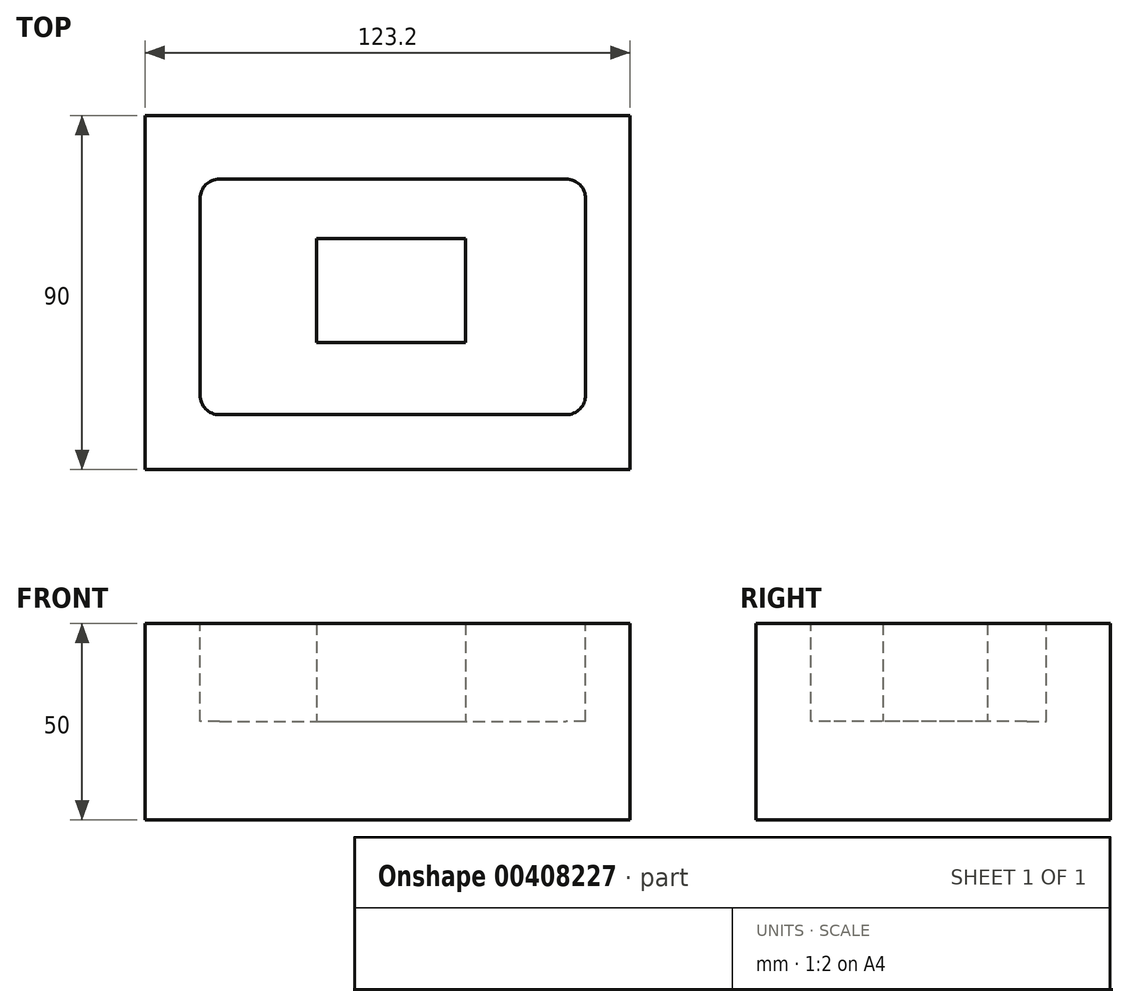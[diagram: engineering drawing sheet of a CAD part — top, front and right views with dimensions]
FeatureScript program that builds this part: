
annotation { "Feature Type Name" : "Feature", "Feature Type Description" : "" }
export const myFeature = defineFeature(function(context is Context, id is Id, definition is map)
    precondition{}
    {
        {
            var Q0;
            Q0=qCreatedBy(makeId("Top.planeOp"),FACE);
            var sketch = newSketch(context, id + "F0", { "sketchPlane" : qUnion([Q0])});
            skLineSegment(sketch, "E0.bottom", {"start": v(-60.6, 50.44) * mm, "end": v(62.6, 50.44) * mm});
            skLineSegment(sketch, "E0.top", {"start": v(-60.6, -39.56) * mm, "end": v(62.6, -39.56) * mm});
            skLineSegment(sketch, "E0.left", {"start": v(-60.6, 50.44) * mm, "end": v(-60.6, -39.56) * mm});
            skLineSegment(sketch, "E0.right", {"start": v(62.6, 50.44) * mm, "end": v(62.6, -39.56) * mm});
            skSolve(sketch);
        }
        {
            var Q0;
            Q0=makeQuery(id+"F0.imprint","IMPRINT",FACE,{"disambiguationData":[TD([[makeQuery(id+"F0.imprint","IMPRINT",EDGE,{"derivedFrom":sQuery(id+"F0.wireOp",EDGE,"E0.bottom")}),-1.0]])]});
            extrude(context, id + "F1", {"entities" : qUnion([Q0]), "depth" : 50 * mm});
        }
        {
            var Q0;
            Q0=makeQuery(id+"F1.opExtrude","CAP_FACE",FACE,{"disambiguationData":[OSD([sQuery(id+"F0.wireOp",EDGE,"E0.bottom"),sQuery(id+"F0.wireOp",EDGE,"E0.top"),sQuery(id+"F0.wireOp",EDGE,"E0.left"),sQuery(id+"F0.wireOp",EDGE,"E0.right")])],"isStart":false});
            var sketch = newSketch(context, id + "F2", { "sketchPlane" : qUnion([Q0])});
            skLineSegment(sketch, "E1.bottom", {"start": v(-46.63, 34.3) * mm, "end": v(51.35, 34.3) * mm});
            skLineSegment(sketch, "E1.top", {"start": v(-46.63, -25.58) * mm, "end": v(51.35, -25.58) * mm});
            skLineSegment(sketch, "E1.left", {"start": v(-46.63, 34.3) * mm, "end": v(-46.63, -25.58) * mm});
            skLineSegment(sketch, "E1.right", {"start": v(51.35, 34.3) * mm, "end": v(51.35, -25.58) * mm});
            skSolve(sketch);
        }
        {
            var Q0;
            Q0=makeQuery(id+"F2.imprint","IMPRINT",FACE,{"disambiguationData":[TD([[makeQuery(id+"F2.imprint","IMPRINT",EDGE,{"derivedFrom":sQuery(id+"F2.wireOp",EDGE,"E1.bottom")}),-1.0]])]});
            extrude(context, id + "F3", {"entities" : qUnion([Q0]), "operationType" : NewBodyOperationType.REMOVE, "oppositeDirection" : true, "depth" : 25 * mm});
        }
        {
            var Q0;
            Q0=makeQuery(id+"F3.boolean.opBoolean","COPY",FACE,{"derivedFrom":makeQuery(id+"F3.opExtrude","CAP_FACE",FACE,{"disambiguationData":[OSD([sQuery(id+"F2.wireOp",EDGE,"E1.bottom"),sQuery(id+"F2.wireOp",EDGE,"E1.top"),sQuery(id+"F2.wireOp",EDGE,"E1.left"),sQuery(id+"F2.wireOp",EDGE,"E1.right")])],"isStart":false})});
            var sketch = newSketch(context, id + "F4", { "sketchPlane" : qUnion([Q0])});
            skLineSegment(sketch, "E2.bottom", {"start": v(-17.06, 19.23) * mm, "end": v(20.87, 19.23) * mm});
            skLineSegment(sketch, "E2.top", {"start": v(-17.06, -7.26) * mm, "end": v(20.87, -7.26) * mm});
            skLineSegment(sketch, "E2.left", {"start": v(-17.06, 19.23) * mm, "end": v(-17.06, -7.26) * mm});
            skLineSegment(sketch, "E2.right", {"start": v(20.87, 19.23) * mm, "end": v(20.87, -7.26) * mm});
            skSolve(sketch);
        }
        {
            var Q0;
            Q0=makeQuery(id+"F4.imprint","IMPRINT",FACE,{"disambiguationData":[TD([[makeQuery(id+"F4.imprint","IMPRINT",EDGE,{"derivedFrom":sQuery(id+"F4.wireOp",EDGE,"E2.bottom")}),-1.0]])]});
            extrude(context, id + "F5", {"entities" : qUnion([Q0]), "operationType" : NewBodyOperationType.ADD, "depth" : 25 * mm});
        }
        {
            var Q0;
            Q0=makeQuery(id+"F3.boolean.opBoolean","COPY",EDGE,{"derivedFrom":makeQuery(id+"F3.opExtrude","SWEPT_EDGE",EDGE,{"disambiguationData":[OSD([sQuery(id+"F2.wireOp",EDGE,"E1.bottom"),sQuery(id+"F2.wireOp",EDGE,"E1.left")])]})});
            var Q1;
            Q1=makeQuery(id+"F3.boolean.opBoolean","COPY",EDGE,{"derivedFrom":makeQuery(id+"F3.opExtrude","SWEPT_EDGE",EDGE,{"disambiguationData":[OSD([sQuery(id+"F2.wireOp",EDGE,"E1.top"),sQuery(id+"F2.wireOp",EDGE,"E1.left")])]})});
            var Q2;
            Q2=makeQuery(id+"F3.boolean.opBoolean","COPY",EDGE,{"derivedFrom":makeQuery(id+"F3.opExtrude","SWEPT_EDGE",EDGE,{"disambiguationData":[OSD([sQuery(id+"F2.wireOp",EDGE,"E1.top"),sQuery(id+"F2.wireOp",EDGE,"E1.right")])]})});
            var Q3;
            Q3=makeQuery(id+"F3.boolean.opBoolean","COPY",EDGE,{"derivedFrom":makeQuery(id+"F3.opExtrude","SWEPT_EDGE",EDGE,{"disambiguationData":[OSD([sQuery(id+"F2.wireOp",EDGE,"E1.bottom"),sQuery(id+"F2.wireOp",EDGE,"E1.right")])]})});
            fillet(context, id + "F6", {"entities" : qUnion([Q0, Q1, Q2, Q3]), "radius" : 5 * mm, "tangentPropagation" : true, "allowEdgeOverflow" : false});
        }
    });
